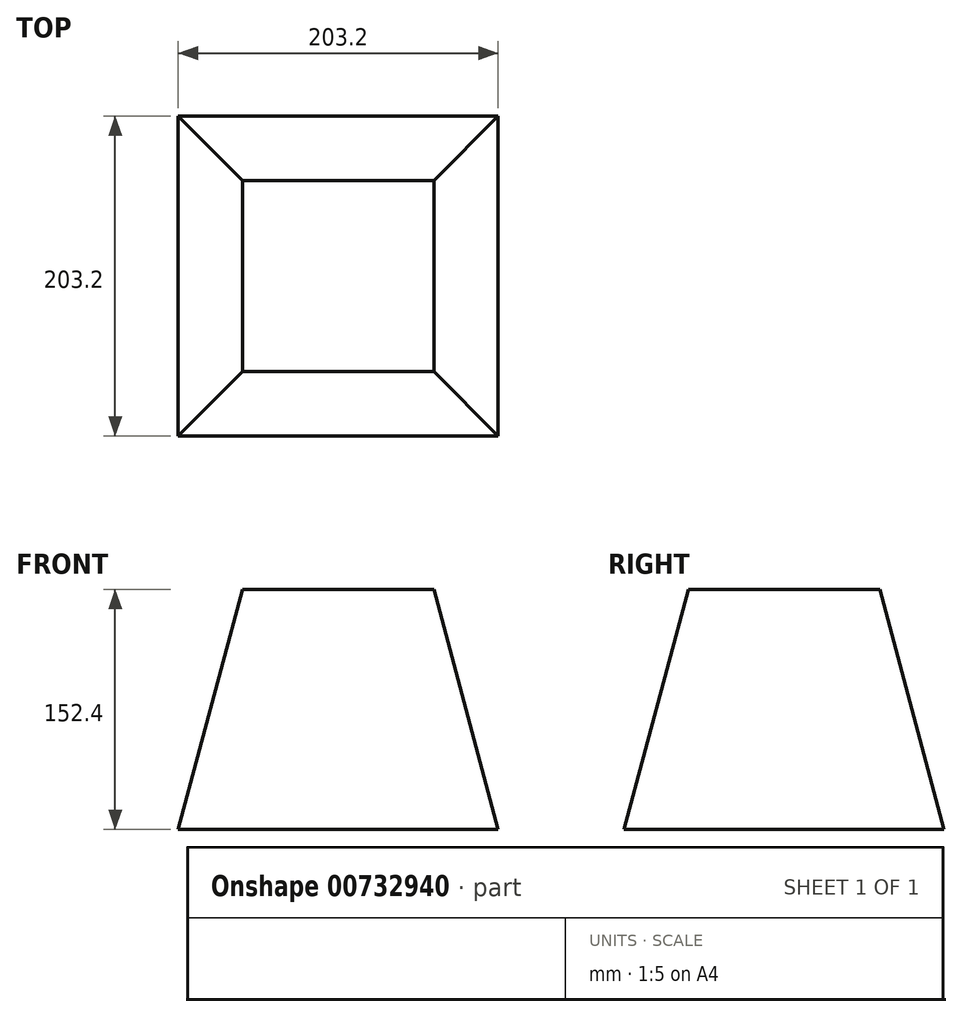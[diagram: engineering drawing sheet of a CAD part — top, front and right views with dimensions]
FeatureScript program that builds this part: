
annotation { "Feature Type Name" : "Feature", "Feature Type Description" : "" }
export const myFeature = defineFeature(function(context is Context, id is Id, definition is map)
    precondition{}
    {
        {
            var Q0;
            Q0=qCreatedBy(makeId("Top.planeOp"),FACE);
            var sketch = newSketch(context, id + "F0", { "sketchPlane" : qUnion([Q0])});
            skLineSegment(sketch, "E0.bottom", {"start": v(101.6, 101.6) * mm, "end": v(-101.6, 101.6) * mm});
            skLineSegment(sketch, "E0.top", {"start": v(101.6, -101.6) * mm, "end": v(-101.6, -101.6) * mm});
            skLineSegment(sketch, "E0.left", {"start": v(101.6, 101.6) * mm, "end": v(101.6, -101.6) * mm});
            skLineSegment(sketch, "E0.right", {"start": v(-101.6, 101.6) * mm, "end": v(-101.6, -101.6) * mm});
            skPoint(sketch, "E0.middle", {"position": v(0, 0) * mm});
            skSolve(sketch);
        }
        {
            var Q0;
            Q0 = qSketchRegion(id + "F0", true);
            extrude(context, id + "F1", {"entities" : qUnion([Q0]), "depth" : 152.4 * mm, "offsetDistance" : 25.4 * mm, "hasDraft" : true, "draftAngle" : 15 * degree, "draftPullDirection" : true});
        }
    });
